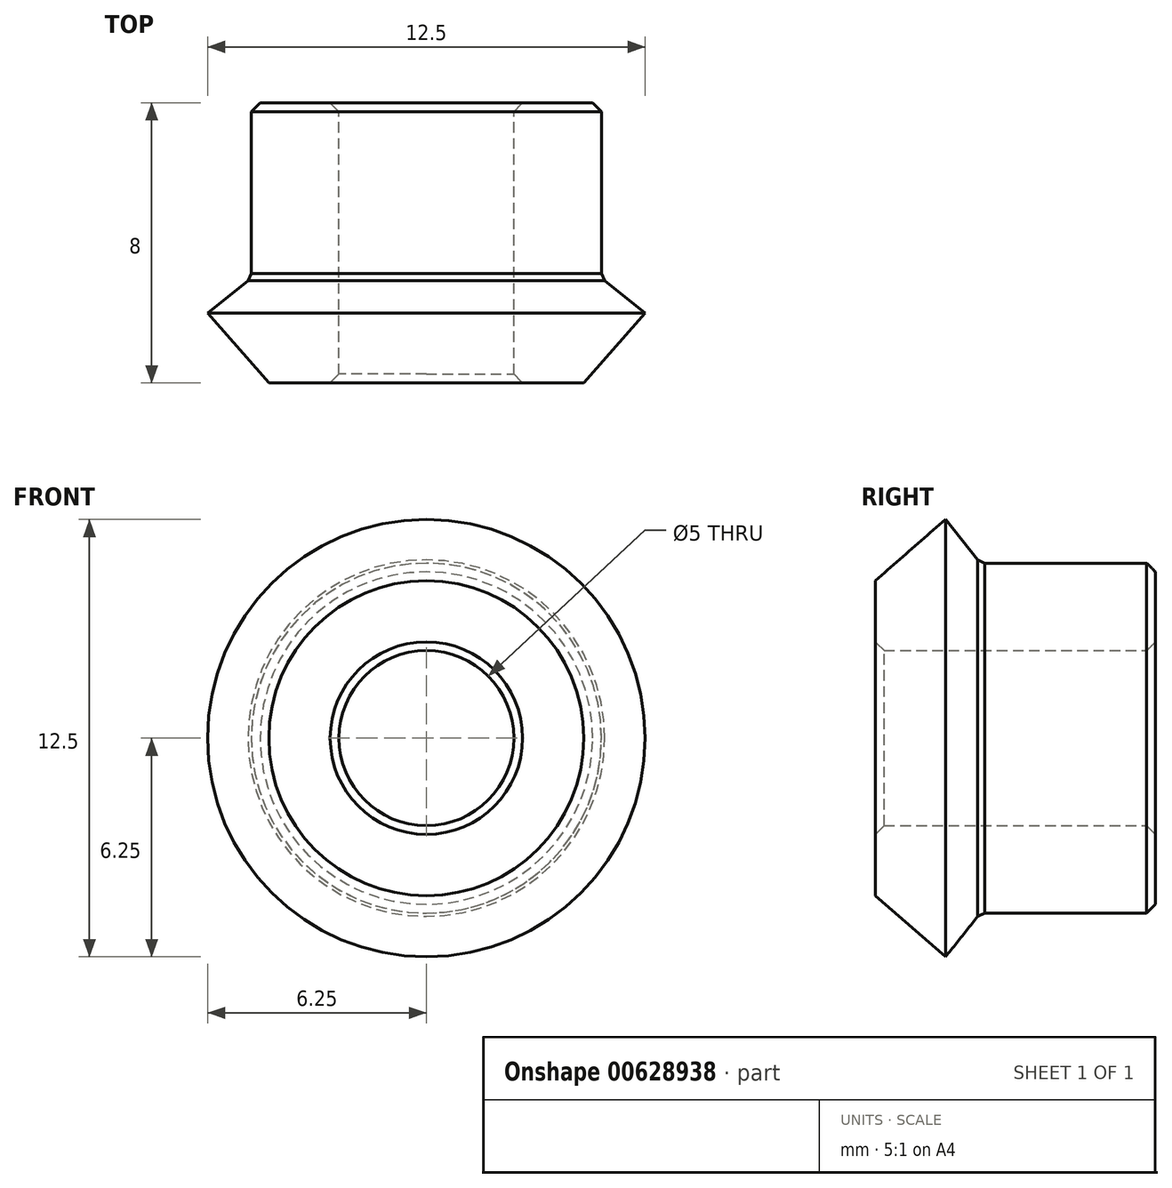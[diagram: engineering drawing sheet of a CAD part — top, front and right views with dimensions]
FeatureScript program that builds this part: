
annotation { "Feature Type Name" : "Feature", "Feature Type Description" : "" }
export const myFeature = defineFeature(function(context is Context, id is Id, definition is map)
    precondition{}
    {
        {
            var Q0;
            Q0=qCreatedBy(makeId("Right.planeOp"),FACE);
            var sketch = newSketch(context, id + "F0", { "sketchPlane" : qUnion([Q0])});
            skLineSegment(sketch, "E0", {"start": v(0, 0) * mm, "end": v(-8, 0) * mm, "construction": true});
            skLineSegment(sketch, "E1", {"start": v(0, -2.5) * mm, "end": v(0, -5) * mm});
            skLineSegment(sketch, "E2", {"start": v(0, -5) * mm, "end": v(-5, -5) * mm});
            skLineSegment(sketch, "E3", {"start": v(-5, -5) * mm, "end": v(-6, -6.25) * mm});
            skLineSegment(sketch, "E4", {"start": v(-6, -6.25) * mm, "end": v(-8, -4.5) * mm});
            skLineSegment(sketch, "E5", {"start": v(-8, -4.5) * mm, "end": v(-8, -2.5) * mm});
            skLineSegment(sketch, "E6", {"start": v(-8, -2.5) * mm, "end": v(0, -2.5) * mm});
            skSolve(sketch);
        }
        {
            var Q0;
            Q0 = qSketchRegion(id + "F0", true);
            var Q1;
            Q1=sQuery(id+"F0.wireOp",EDGE,"E0");
            revolve(context, id + "F1", {"entities" : qUnion([Q0]), "axis" : qUnion([Q1]), "revolveType" : RevolveType.FULL});
        }
        {
            var Q0;
            Q0=makeQuery(id+"F1.opRevolve","SWEPT_EDGE",EDGE,{"disambiguationData":[OSD([sQuery(id+"F0.wireOp",EDGE,"E5"),sQuery(id+"F0.wireOp",EDGE,"E6")])]});
            var Q1;
            Q1=makeQuery(id+"F1.opRevolve","SWEPT_EDGE",EDGE,{"disambiguationData":[OSD([sQuery(id+"F0.wireOp",EDGE,"E1"),sQuery(id+"F0.wireOp",EDGE,"E6")])]});
            var Q2;
            Q2=makeQuery(id+"F1.opRevolve","SWEPT_EDGE",EDGE,{"disambiguationData":[OSD([sQuery(id+"F0.wireOp",EDGE,"E1"),sQuery(id+"F0.wireOp",EDGE,"E2")])]});
            var Q3;
            Q3=makeQuery(id+"F1.opRevolve","SWEPT_EDGE",EDGE,{"disambiguationData":[OSD([sQuery(id+"F0.wireOp",EDGE,"E2"),sQuery(id+"F0.wireOp",EDGE,"E3")])]});
            chamfer(context, id + "F2", {"entities" : qUnion([Q0, Q1, Q2, Q3]), "width" : 0.25 * mm, "tangentPropagation" : true});
        }
    });
